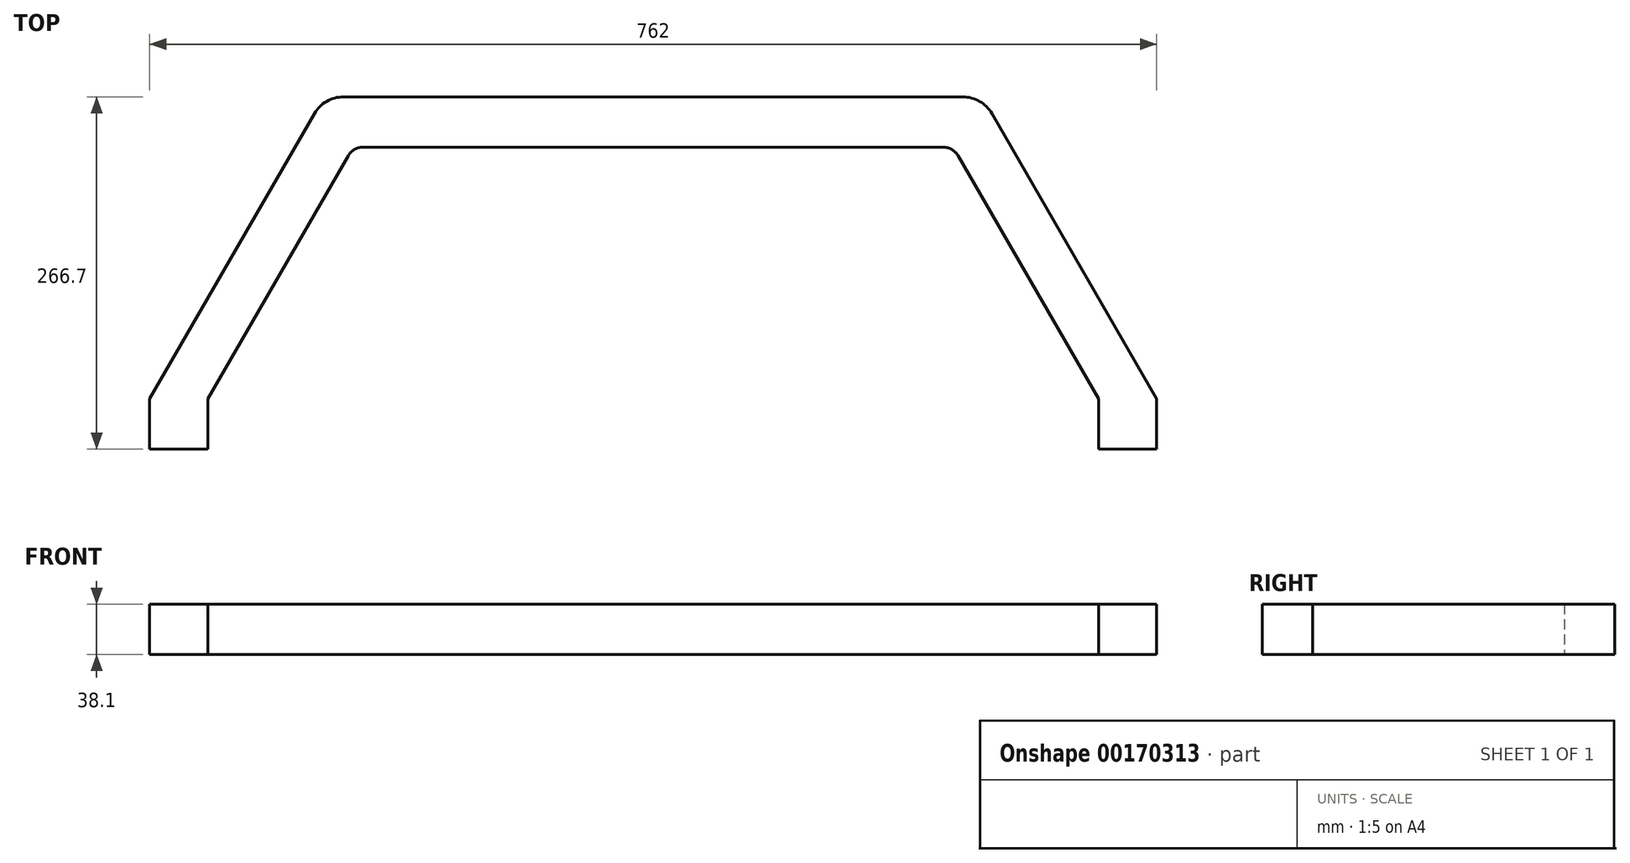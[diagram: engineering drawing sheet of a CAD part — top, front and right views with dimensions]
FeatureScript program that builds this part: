
annotation { "Feature Type Name" : "Feature", "Feature Type Description" : "" }
export const myFeature = defineFeature(function(context is Context, id is Id, definition is map)
    precondition{}
    {
        {
            var Q0;
            Q0=qCreatedBy(makeId("Top.planeOp"),FACE);
            var sketch = newSketch(context, id + "F0", { "sketchPlane" : qUnion([Q0])});
            skLineSegment(sketch, "E0", {"start": v(-369.78, -74.71) * mm, "end": v(-245.13, 141.19) * mm});
            skLineSegment(sketch, "E1", {"start": v(-223.13, 153.89) * mm, "end": v(245.57, 153.89) * mm});
            skLineSegment(sketch, "E2", {"start": v(267.57, 141.19) * mm, "end": v(392.22, -74.71) * mm});
            skLineSegment(sketch, "E3", {"start": v(-208.47, 115.79) * mm, "end": v(230.9, 115.79) * mm});
            skLineSegment(sketch, "E4", {"start": v(-219.47, 109.44) * mm, "end": v(-325.79, -74.71) * mm});
            skLineSegment(sketch, "E5", {"start": v(241.9, 109.44) * mm, "end": v(348.23, -74.71) * mm});
            skLineSegment(sketch, "E6", {"start": v(-369.78, -74.71) * mm, "end": v(-325.79, -74.71) * mm});
            skLineSegment(sketch, "E7", {"start": v(348.23, -74.71) * mm, "end": v(392.22, -74.71) * mm});
            skPoint(sketch, "E8.visualSharp", {"position": v(-237.8, 153.89) * mm});
            skArc(sketch, "E8.filletArc", {"start": v(-223.13, 153.89) * mm, "mid": v(-235.83, 150.49) * mm, "end": v(-245.13, 141.19) * mm});
            skPoint(sketch, "E9.visualSharp", {"position": v(260.24, 153.89) * mm});
            skArc(sketch, "E9.filletArc", {"start": v(267.57, 141.19) * mm, "mid": v(258.27, 150.49) * mm, "end": v(245.57, 153.89) * mm});
            skPoint(sketch, "E10.visualSharp", {"position": v(-215.8, 115.79) * mm});
            skArc(sketch, "E10.filletArc", {"start": v(-208.47, 115.79) * mm, "mid": v(-214.82, 114.09) * mm, "end": v(-219.47, 109.44) * mm});
            skPoint(sketch, "E11.visualSharp", {"position": v(238.24, 115.79) * mm});
            skArc(sketch, "E11.filletArc", {"start": v(241.9, 109.44) * mm, "mid": v(237.26, 114.09) * mm, "end": v(230.9, 115.79) * mm});
            skLineSegment(sketch, "E12", {"start": v(-369.78, -74.71) * mm, "end": v(-369.78, -112.81) * mm});
            skLineSegment(sketch, "E13", {"start": v(-369.78, -112.81) * mm, "end": v(-325.79, -112.81) * mm});
            skLineSegment(sketch, "E14", {"start": v(-325.79, -112.81) * mm, "end": v(-325.79, -74.71) * mm});
            skLineSegment(sketch, "E15", {"start": v(348.23, -74.71) * mm, "end": v(348.23, -112.81) * mm});
            skLineSegment(sketch, "E16", {"start": v(348.23, -112.81) * mm, "end": v(392.22, -112.81) * mm});
            skLineSegment(sketch, "E17", {"start": v(392.22, -112.81) * mm, "end": v(392.22, -74.71) * mm});
            skSolve(sketch);
        }
        {
            var Q0;
            Q0 = qSketchRegion(id + "F0", true);
            extrude(context, id + "F1", {"entities" : qUnion([Q0]), "depth" : 38.1 * mm});
        }
    });
